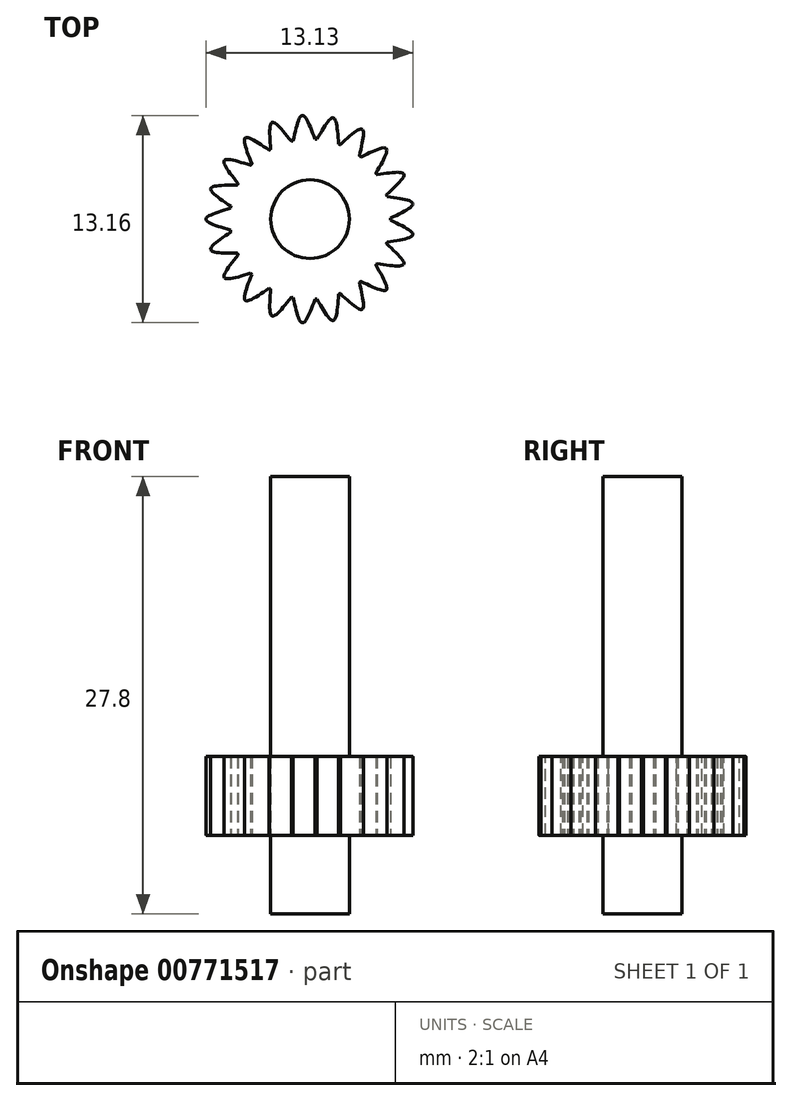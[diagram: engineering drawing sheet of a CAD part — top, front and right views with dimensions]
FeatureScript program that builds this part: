
annotation { "Feature Type Name" : "Feature", "Feature Type Description" : "" }
export const myFeature = defineFeature(function(context is Context, id is Id, definition is map)
    precondition{}
    {
        {
            var Q0;
            Q0=qCreatedBy(makeId("Top.planeOp"),FACE);
            var sketch = newSketch(context, id + "F0", { "sketchPlane" : qUnion([Q0])});
            skLineSegment(sketch, "E0", {"start": v(0, 0) * mm, "end": v(5.1, 0) * mm, "construction": true});
            skLineSegment(sketch, "E1", {"start": v(5.1, 0) * mm, "end": v(-6.6, 0) * mm, "construction": true});
            skCircle(sketch, "E2", {"center": v(0, 0) * mm, "radius": 2.5 * mm});
            skCircle(sketch, "E3", {"center": v(0, 0) * mm, "radius": 5.1 * mm});
            skLineSegment(sketch, "E4", {"start": v(-5.1, 0) * mm, "end": v(-5.1, 0.7) * mm, "construction": true});
            skLineSegment(sketch, "E5", {"start": v(-5.1, 0.7) * mm, "end": v(-5.1, -0.7) * mm, "construction": true});
            skLineSegment(sketch, "E6", {"start": v(-5.1, -0.7) * mm, "end": v(-5.05, -0.7) * mm, "construction": true});
            skLineSegment(sketch, "E7", {"start": v(-5.05, -0.7) * mm, "end": v(-5.05, 0.7) * mm, "construction": true});
            skLineSegment(sketch, "E8", {"start": v(-5.05, 0.7) * mm, "end": v(-5.1, 0.7) * mm, "construction": true});
            skFitSpline(sketch, "E9", {"points": [v(-5.05, -0.7) * mm, v(-6.6, 0) * mm, v(-5.05, 0.7) * mm], "startDerivative": vector(-4.69, 1.4) * mm, "endDerivative": vector(4.69, 1.4) * mm});
            skSolve(sketch);
        }
        {
            var Q0;
            Q0=makeQuery(id+"F0.imprint","IMPRINT",FACE,{"disambiguationData":[TD([[makeQuery(id+"F0.imprint","IMPRINT",EDGE,{"derivedFrom":sQuery(id+"F0.wireOp",EDGE,"E2")}),-1.0]])]});
            var Q1;
            {var subQ0=sQuery(id+"F0.wireOp",EDGE,"E9");Q1=makeQuery(id+"F0.imprint","IMPRINT",FACE,{"disambiguationData":[TD([[makeQuery(id+"F0.imprint","IMPRINT",EDGE,{"derivedFrom":subQ0}),-1.0]])]});}
            extrude(context, id + "F1", {"entities" : qUnion([Q0, Q1]), "depth" : 5 * mm, "offsetDistance" : 25 * mm});
        }
        {
            var Q0;
            Q0=makeQuery(id+"F1.opExtrude","SWEPT_BODY",BODY,{"disambiguationData":[OSD([sQuery(id+"F0.wireOp",EDGE,"E2"),sQuery(id+"F0.wireOp",EDGE,"E3"),sQuery(id+"F0.wireOp",EDGE,"E9")])]});
            var Q1;
            Q1=makeQuery(id+"F1.opExtrude","CAP_EDGE",EDGE,{"disambiguationData":[OSD([sQuery(id+"F0.wireOp",EDGE,"E2")])],"isStart":false});
            circularPattern(context, id + "F2", {"entities" : qUnion([Q0]), "axis" : qUnion([Q1]), "angle" : 360 * degree, "instanceCount" : 21, "equalSpace" : true});
        }
        {
            var Q0;
            Q0=makeQuery(id+"F0.imprint","IMPRINT",FACE,{"disambiguationData":[TD([[makeQuery(id+"F0.imprint","IMPRINT",EDGE,{"derivedFrom":sQuery(id+"F0.wireOp",EDGE,"E2")}),1.0]])]});
            extrude(context, id + "F3", {"entities" : qUnion([Q0]), "operationType" : NewBodyOperationType.ADD, "depth" : 22.8 * mm, "offsetDistance" : 25 * mm});
        }
        {
            var Q0;
            Q0=makeQuery(id+"F0.imprint","IMPRINT",FACE,{"disambiguationData":[TD([[makeQuery(id+"F0.imprint","IMPRINT",EDGE,{"derivedFrom":sQuery(id+"F0.wireOp",EDGE,"E2")}),1.0]])]});
            extrude(context, id + "F4", {"entities" : qUnion([Q0]), "operationType" : NewBodyOperationType.ADD, "oppositeDirection" : true, "depth" : 5 * mm, "offsetDistance" : 25 * mm});
        }
    });
